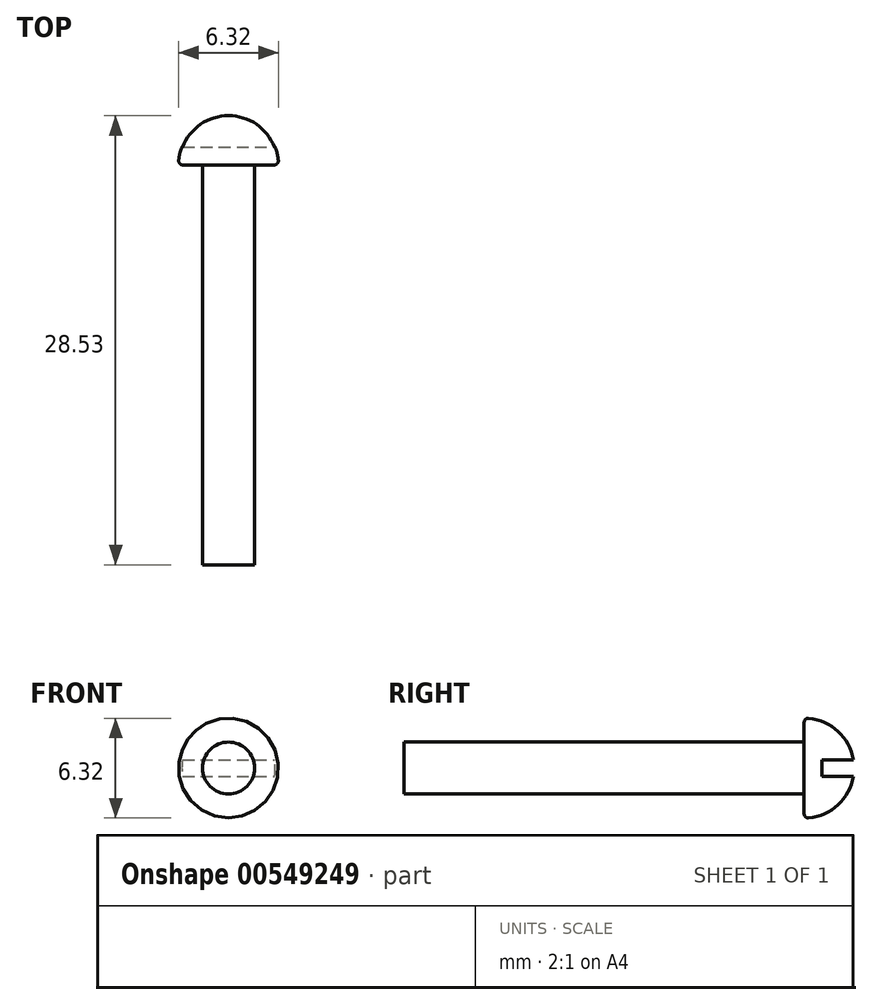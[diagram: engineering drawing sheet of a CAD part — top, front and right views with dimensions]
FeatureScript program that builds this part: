
annotation { "Feature Type Name" : "Feature", "Feature Type Description" : "" }
export const myFeature = defineFeature(function(context is Context, id is Id, definition is map)
    precondition{}
    {
        {
            var Q0;
            Q0=qCreatedBy(makeId("Front.planeOp"),FACE);
            var sketch = newSketch(context, id + "F0", { "sketchPlane" : qUnion([Q0])});
            skCircle(sketch, "E0", {"center": v(0, 0) * mm, "radius": 1.65 * mm});
            skSolve(sketch);
        }
        {
            var Q0;
            Q0=makeQuery(id+"F0.imprint","IMPRINT",FACE,{"disambiguationData":[TD([[makeQuery(id+"F0.imprint","IMPRINT",EDGE,{"derivedFrom":sQuery(id+"F0.wireOp",EDGE,"E0")}),1.0]])]});
            extrude(context, id + "F1", {"entities" : qUnion([Q0]), "depth" : 25.4 * mm, "offsetDistance" : 25.4 * mm});
        }
        {
            var Q0;
            Q0=qCreatedBy(makeId("Right.planeOp"),FACE);
            var sketch = newSketch(context, id + "F2", { "sketchPlane" : qUnion([Q0])});
            skLineSegment(sketch, "E1", {"start": v(0, 0) * mm, "end": v(0, 2.9) * mm});
            skArc(sketch, "E2", {"start": v(3.17, 0) * mm, "mid": v(2.34, 2.15) * mm, "end": v(0.28, 3.16) * mm});
            skLineSegment(sketch, "E3", {"start": v(0, 0) * mm, "end": v(3.17, 0) * mm});
            skPoint(sketch, "E4.visualSharp", {"position": v(0, 3.17) * mm});
            skArc(sketch, "E4.filletArc", {"start": v(0.28, 3.16) * mm, "mid": v(0.08, 3.1) * mm, "end": v(0, 2.9) * mm});
            skSolve(sketch);
        }
        {
            var Q0;
            Q0=makeQuery(id+"F2.imprint","IMPRINT",FACE,{"disambiguationData":[TD([[makeQuery(id+"F2.imprint","IMPRINT",EDGE,{"derivedFrom":sQuery(id+"F2.wireOp",EDGE,"E1")}),-1.0]])]});
            var Q1;
            Q1=sQuery(id+"F2.wireOp",EDGE,"E3");
            revolve(context, id + "F3", {"operationType" : NewBodyOperationType.ADD, "entities" : qUnion([Q0]), "axis" : qUnion([Q1]), "revolveType" : RevolveType.FULL});
        }
        {
            var Q0;
            Q0=qCreatedBy(makeId("Right.planeOp"),FACE);
            var sketch = newSketch(context, id + "F4", { "sketchPlane" : qUnion([Q0])});
            skLineSegment(sketch, "E5.bottom", {"start": v(1.13, 0.52) * mm, "end": v(4.25, 0.52) * mm});
            skLineSegment(sketch, "E5.top", {"start": v(1.13, -0.52) * mm, "end": v(4.25, -0.52) * mm});
            skLineSegment(sketch, "E5.left", {"start": v(1.13, 0.52) * mm, "end": v(1.13, -0.52) * mm});
            skLineSegment(sketch, "E5.right", {"start": v(4.25, 0.52) * mm, "end": v(4.25, -0.52) * mm});
            skPoint(sketch, "E5.middle", {"position": v(2.7, 0) * mm});
            skSolve(sketch);
        }
        {
            var Q0;
            Q0=makeQuery(id+"F4.imprint","IMPRINT",FACE,{"disambiguationData":[TD([[makeQuery(id+"F4.imprint","IMPRINT",EDGE,{"derivedFrom":sQuery(id+"F4.wireOp",EDGE,"E5.bottom")}),-1.0]])]});
            extrude(context, id + "F5", {"entities" : qUnion([Q0]), "operationType" : NewBodyOperationType.REMOVE, "endBound" : BoundingType.SYMMETRIC, "oppositeDirection" : true, "depth" : 25.4 * mm, "offsetDistance" : 25.4 * mm});
        }
    });
